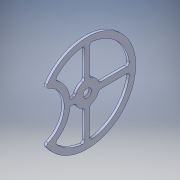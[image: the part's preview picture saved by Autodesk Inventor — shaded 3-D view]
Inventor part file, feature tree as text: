
AUTODESK INVENTOR PART (.ipt)
format: ipt  version: 2016 (Build 200138000, 138)  size: 646,656 bytes
history: native  units: in
note: dims shown in document units (in); Inventor stores cm internally (conversion verified against a paired STEP export)
features: sketch x1, other x1
ambient origin geometry x8: Origin, YZ Plane, XZ Plane, XY Plane, X Axis, Y Axis, Z Axis, Center Point
bodies: Solid1 (feature_tree)
feature tree (2):
  sketch  "Sketch1"
  other  "Cut-Extrude1"
